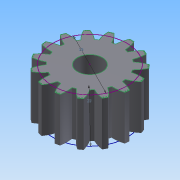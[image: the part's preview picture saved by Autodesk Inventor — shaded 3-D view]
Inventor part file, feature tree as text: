
AUTODESK INVENTOR PART (.ipt)
format: ipt  version: 2015 (Build 190159000, 159)  size: 236,032 bytes
history: native  units: mm (DEFAULTED — no unit token found)
features: sketch x4, plane x3, other x3, extrude x2, projected_geometry x1
ambient origin geometry x8: Origin, YZ Plane, XZ Plane, XY Plane, X Axis, Y Axis, Z Axis, Center Point
bodies: Solid1 (feature_tree)
feature tree (13):
  extrude  "Extrusion1"  Depth=9.0mm TaperAngle=0.0deg
  plane  "Work Plane2"
  plane  "Work Plane8"
  plane  "Work Plane9"
  other  "Spur Gear"
  extrude  "Extrusion2"  Depth=10.0mm TaperAngle=0.0deg
  sketch  "Sketch4"  dims[d17=0.0mm d34=2.094395mm d39=0.0mm d41=0.0mm d43=15.0mm d46=15.0mm d47=0.0mm d48=0.0mm d49=5.0mm d50=10.0mm d51=0.0mm d52=15.0mm d53=15.0mm]
  sketch  "Sketch1"  dims[d0=17.0mm d1=9.0mm d2=0.0mm]
  sketch  "Sketch2"  dims[d3=15.0mm d4=10.0mm d5=0.0mm]
  other  "Srf1"
  sketch  "Sketch3"  dims[d16=15.0mm]
  projected_geometry  "Projected Loop1"
  other  "Pitch Diameter"
